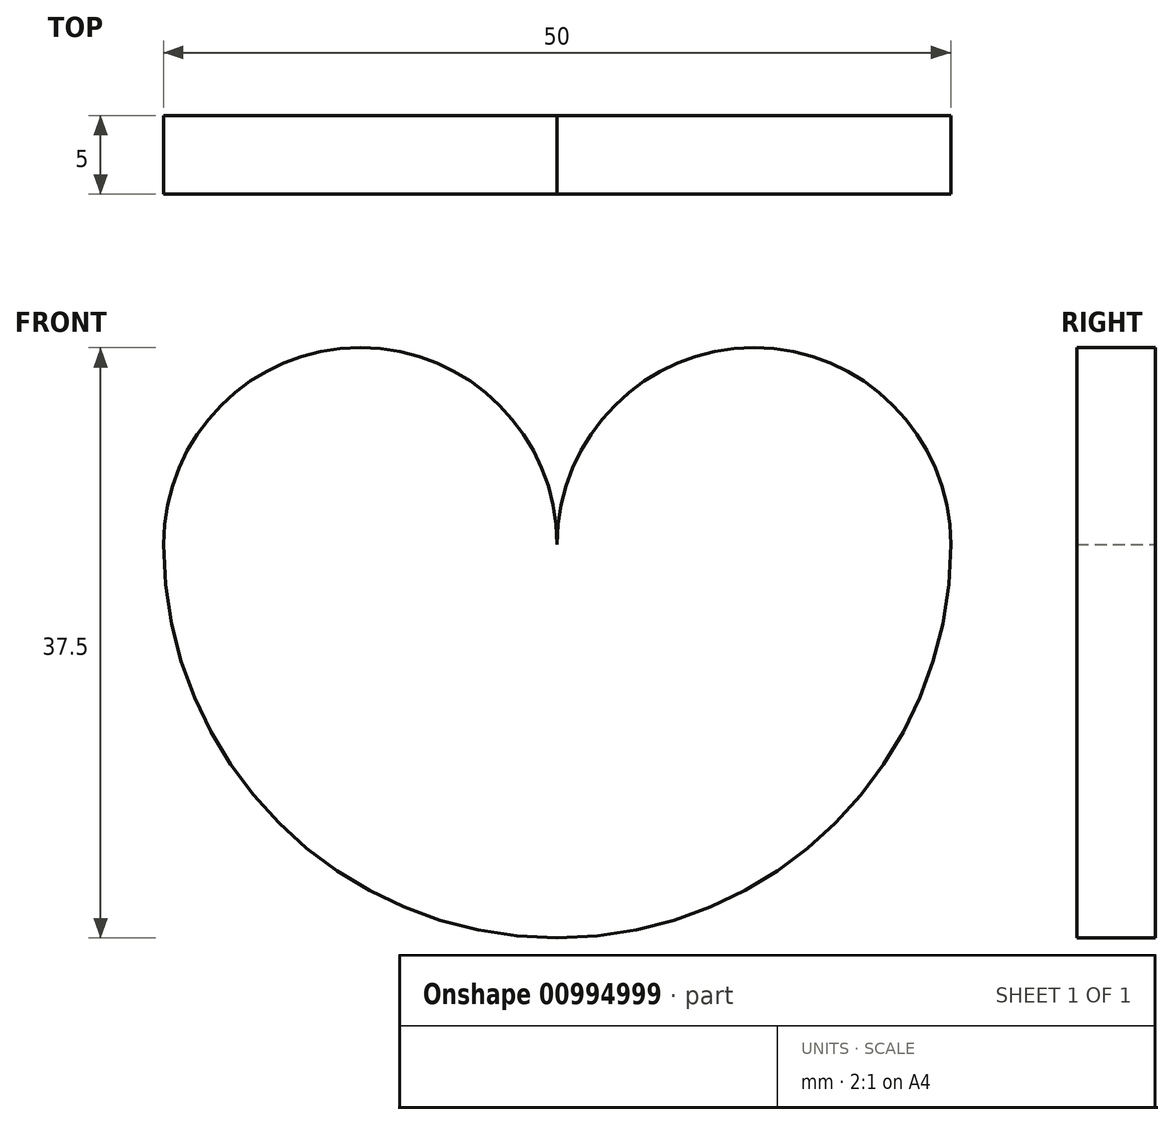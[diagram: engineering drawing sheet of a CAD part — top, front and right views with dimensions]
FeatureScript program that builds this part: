
annotation { "Feature Type Name" : "Feature", "Feature Type Description" : "" }
export const myFeature = defineFeature(function(context is Context, id is Id, definition is map)
    precondition{}
    {
        {
            var Q0;
            Q0=qCreatedBy(makeId("Front.planeOp"),FACE);
            var sketch = newSketch(context, id + "F0", { "sketchPlane" : qUnion([Q0])});
            skArc(sketch, "E0", {"start": v(-25, 0) * mm, "mid": v(0, -25) * mm, "end": v(25, 0) * mm});
            skPoint(sketch, "E1", {"position": v(-12.5, 0) * mm});
            skPoint(sketch, "E2", {"position": v(12.5, 0) * mm});
            skArc(sketch, "E3", {"start": v(0, 0) * mm, "mid": v(-12.5, 12.5) * mm, "end": v(-25, 0) * mm});
            skArc(sketch, "E4", {"start": v(25, 0) * mm, "mid": v(12.5, 12.5) * mm, "end": v(0, 0) * mm});
            skSolve(sketch);
        }
        {
            var Q0;
            Q0=makeQuery(id+"F0.imprint","IMPRINT",FACE,{"disambiguationData":[TD([[makeQuery(id+"F0.imprint","IMPRINT",EDGE,{"derivedFrom":sQuery(id+"F0.wireOp",EDGE,"E0")}),1.0]])]});
            extrude(context, id + "F1", {"entities" : qUnion([Q0]), "depth" : 5 * mm, "offsetDistance" : 25 * mm});
        }
    });
